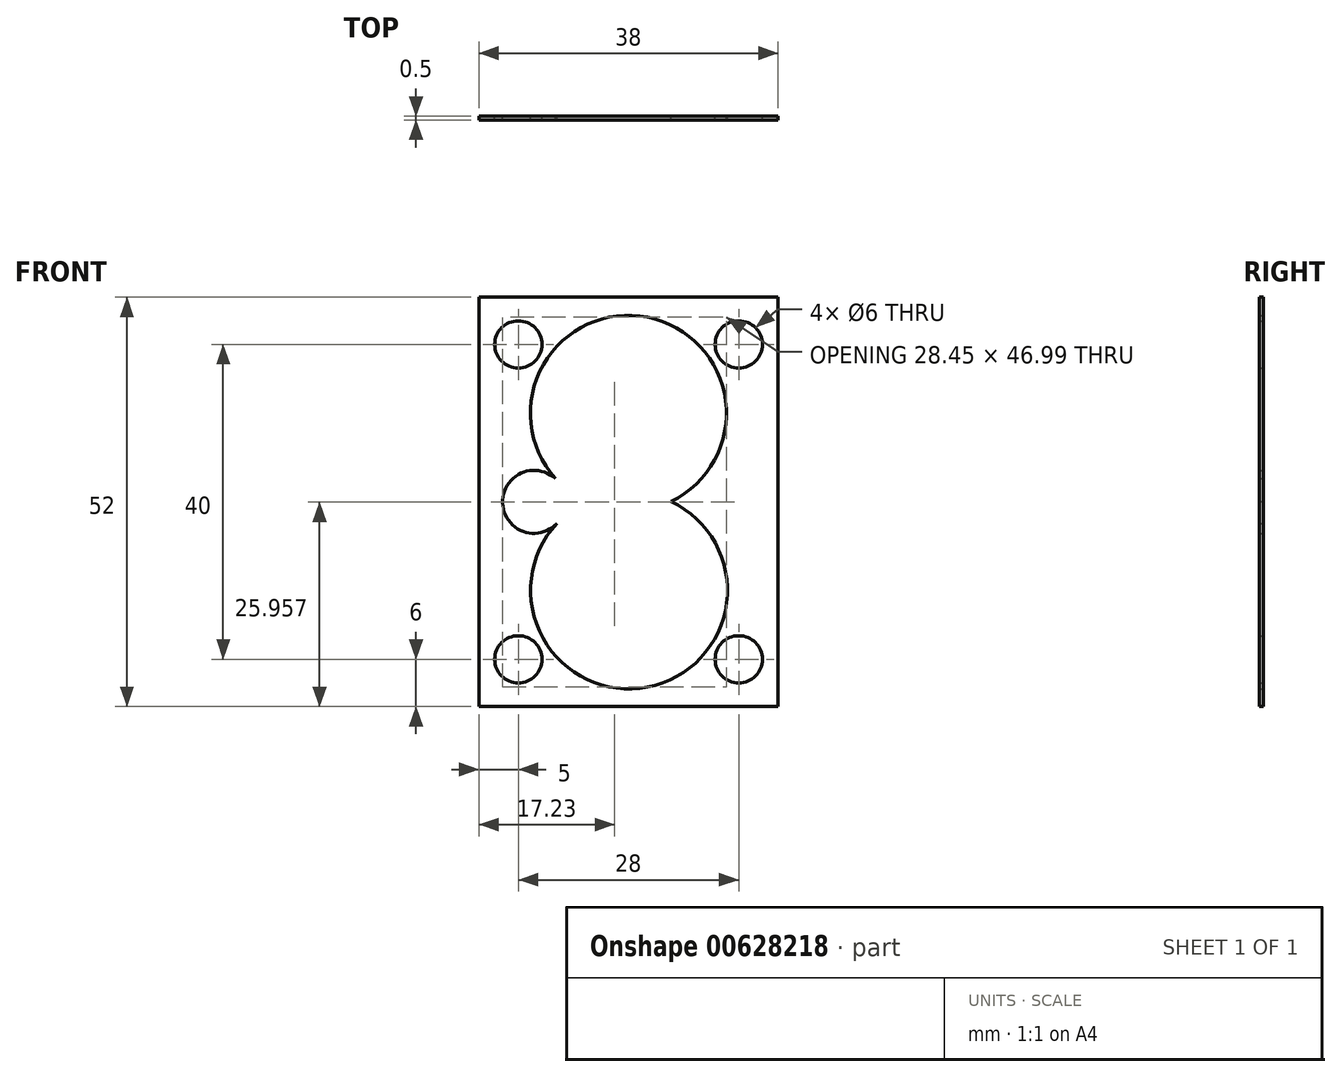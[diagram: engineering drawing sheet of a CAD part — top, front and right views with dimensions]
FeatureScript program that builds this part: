
annotation { "Feature Type Name" : "Feature", "Feature Type Description" : "" }
export const myFeature = defineFeature(function(context is Context, id is Id, definition is map)
    precondition{}
    {
        {
            var Q0;
            Q0=qCreatedBy(makeId("Front.planeOp"),FACE);
            var sketch = newSketch(context, id + "F0", { "sketchPlane" : qUnion([Q0])});
            skPoint(sketch, "E0.middle", {"position": v(0, 0) * mm});
            skCircle(sketch, "E1", {"center": v(-14, 20) * mm, "radius": 3 * mm});
            skLineSegment(sketch, "E2.bottom", {"start": v(-19, 26) * mm, "end": v(19, 26) * mm});
            skLineSegment(sketch, "E2.top", {"start": v(-19, -26) * mm, "end": v(19, -26) * mm});
            skLineSegment(sketch, "E2.left", {"start": v(-19, 26) * mm, "end": v(-19, -26) * mm});
            skLineSegment(sketch, "E2.right", {"start": v(19, 26) * mm, "end": v(19, -26) * mm});
            skCircle(sketch, "E3", {"center": v(14, 20) * mm, "radius": 3 * mm});
            skCircle(sketch, "E4", {"center": v(14, -20) * mm, "radius": 3 * mm});
            skCircle(sketch, "E5", {"center": v(-14, -20) * mm, "radius": 3 * mm});
            skArc(sketch, "E6", {"start": v(-9.3, 2.96) * mm, "mid": v(-16, -0.16) * mm, "end": v(-9.08, -2.73) * mm});
            skArc(sketch, "E7", {"start": v(5.4, 0.04) * mm, "mid": v(2.4, 23.45) * mm, "end": v(-9.3, 2.96) * mm});
            skArc(sketch, "E8", {"start": v(-9.08, -2.73) * mm, "mid": v(2.4, -23.54) * mm, "end": v(5.4, 0.04) * mm});
            skSolve(sketch);
        }
        {
            var Q0;
            Q0=makeQuery(id+"F0.imprint","IMPRINT",FACE,{"disambiguationData":[TD([[makeQuery(id+"F0.imprint","IMPRINT",EDGE,{"derivedFrom":sQuery(id+"F0.wireOp",EDGE,"E1")}),-1.0]])]});
            extrude(context, id + "F1", {"entities" : qUnion([Q0]), "depth" : 0.5 * mm, "offsetDistance" : 25 * mm});
        }
    });
